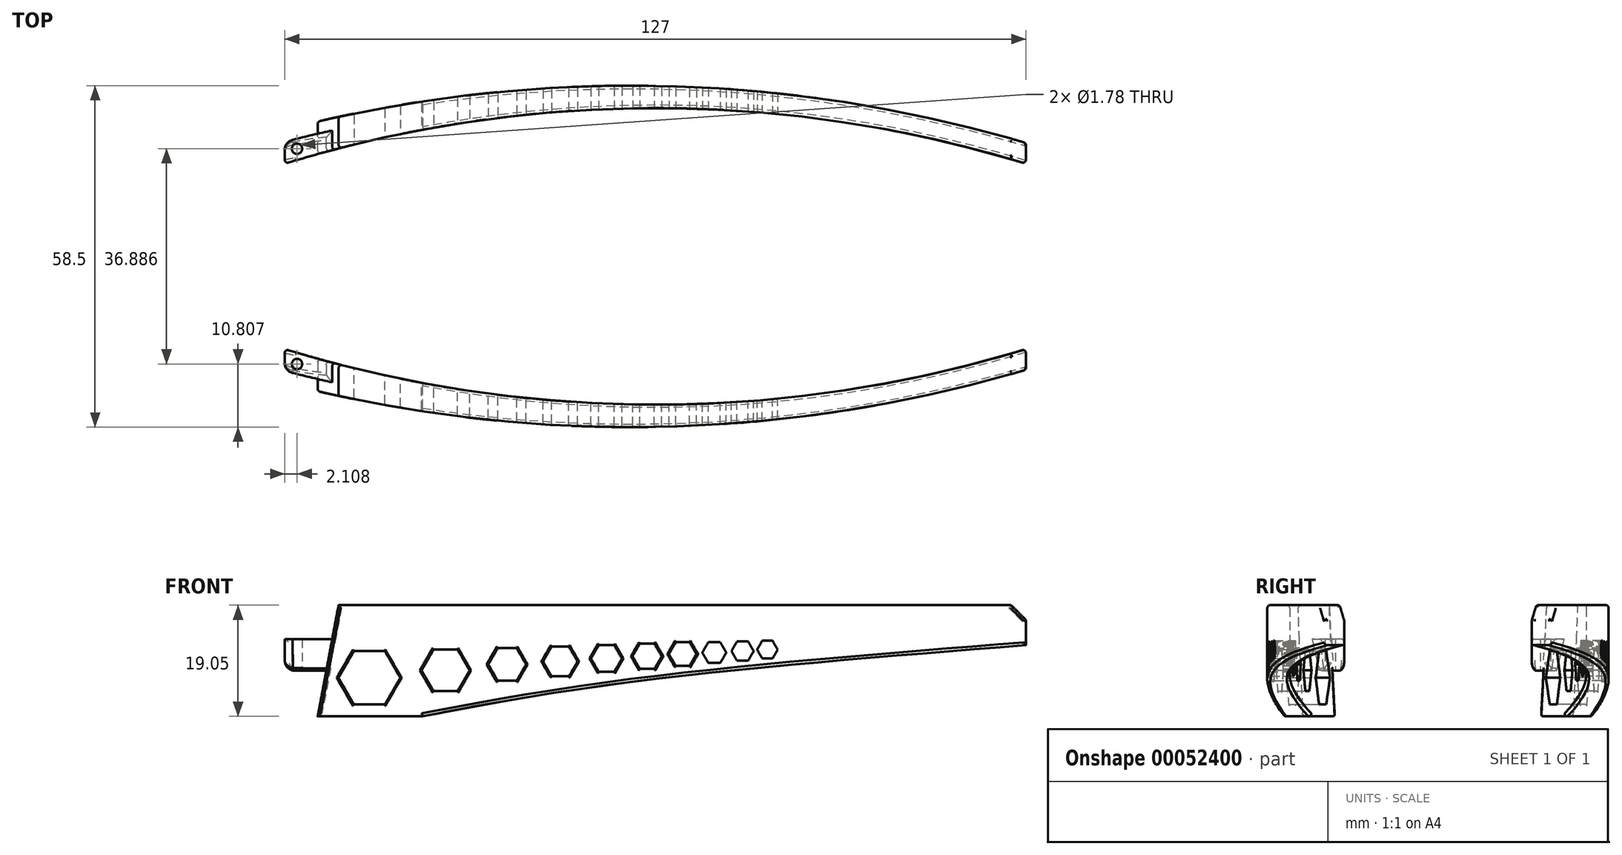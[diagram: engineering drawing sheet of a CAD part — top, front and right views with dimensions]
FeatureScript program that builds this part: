
annotation { "Feature Type Name" : "Feature", "Feature Type Description" : "" }
export const myFeature = defineFeature(function(context is Context, id is Id, definition is map)
    precondition{}
    {
        {
            var Q0;
            Q0=qCreatedBy(makeId("Top.planeOp"),FACE);
            var sketch = newSketch(context, id + "F0", { "sketchPlane" : qUnion([Q0])});
            skLineSegment(sketch, "E0.bottom", {"start": v(0, 0) * mm, "end": v(127, 0) * mm});
            skLineSegment(sketch, "E0.top", {"start": v(0, -9.53) * mm, "end": v(127, -9.53) * mm});
            skLineSegment(sketch, "E0.left", {"start": v(0, 0) * mm, "end": v(0, -9.53) * mm});
            skLineSegment(sketch, "E0.right", {"start": v(127, 0) * mm, "end": v(127, -9.53) * mm});
            skPoint(sketch, "E1", {"position": v(63.5, 0) * mm});
            skArc(sketch, "E2", {"start": v(127, -9.53) * mm, "mid": v(63.5, 0) * mm, "end": v(0, -9.53) * mm});
            skPoint(sketch, "E3", {"position": v(0, -3.68) * mm});
            skPoint(sketch, "E4", {"position": v(63.5, 3.81) * mm});
            skPoint(sketch, "E5", {"position": v(127, -5.97) * mm});
            skArc(sketch, "E6", {"start": v(127, -5.97) * mm, "mid": v(63.66, 3.8) * mm, "end": v(0, -3.68) * mm});
            skSolve(sketch);
        }
        {
            var Q0;
            {var subQ0=sQuery(id+"F0.wireOp",EDGE,"E6");var subQ1=sQuery(id+"F0.wireOp",EDGE,"E0.bottom");var subQ2=makeQuery(id+"F0.imprint","INTERSECT",VERTEX,{"disambiguationData":[OD(0.0)],"derivedFrom":[subQ1,subQ0]});Q0=makeQuery(id+"F0.imprint","IMPRINT",FACE,{"disambiguationData":[TD([[makeQuery(id+"F0.imprint","IMPRINT",EDGE,{"disambiguationData":[TD([[subQ2,-1.0]])],"derivedFrom":subQ1}),1.0]])]});}
            var Q1;
            {var subQ0=sQuery(id+"F0.wireOp",EDGE,"E6");var subQ1=sQuery(id+"F0.wireOp",EDGE,"E0.bottom");var subQ2=makeQuery(id+"F0.imprint","INTERSECT",VERTEX,{"disambiguationData":[OD(0.0)],"derivedFrom":[subQ1,subQ0]});Q1=makeQuery(id+"F0.imprint","IMPRINT",FACE,{"disambiguationData":[TD([[makeQuery(id+"F0.imprint","IMPRINT",EDGE,{"disambiguationData":[TD([[subQ2,-1.0]])],"derivedFrom":subQ1}),-1.0]])]});}
            var Q2;
            {var subQ0=sQuery(id+"F0.wireOp",EDGE,"E6");var subQ1=sQuery(id+"F0.wireOp",EDGE,"E0.bottom");var subQ2=makeQuery(id+"F0.imprint","INTERSECT",VERTEX,{"disambiguationData":[OD(1.0)],"derivedFrom":[subQ1,subQ0]});Q2=makeQuery(id+"F0.imprint","IMPRINT",FACE,{"disambiguationData":[TD([[makeQuery(id+"F0.imprint","IMPRINT",EDGE,{"disambiguationData":[TD([[subQ2,1.0]])],"derivedFrom":subQ1}),-1.0]])]});}
            extrude(context, id + "F1", {"entities" : qUnion([Q0, Q1, Q2]), "depth" : 19.05 * mm});
        }
        {
            var Q0;
            Q0=qCreatedBy(makeId("Front.planeOp"),FACE);
            var sketch = newSketch(context, id + "F2", { "sketchPlane" : qUnion([Q0])});
            skLineSegment(sketch, "E7.0.0", {"start": v(127, 0) * mm, "end": v(0, 0) * mm});
            skLineSegment(sketch, "E7.0.1", {"start": v(127, 0) * mm, "end": v(127, 19.05) * mm});
            skLineSegment(sketch, "E7.0.2", {"start": v(0, 19.05) * mm, "end": v(127, 19.05) * mm});
            skLineSegment(sketch, "E7.0.3", {"start": v(0, 19.05) * mm, "end": v(0, 0) * mm});
            skPoint(sketch, "E8", {"position": v(7.11, 7.82) * mm});
            skPoint(sketch, "E9", {"position": v(8.13, 13.2) * mm});
            skLineSegment(sketch, "E10", {"start": v(8.13, 13.2) * mm, "end": v(0, 13.2) * mm});
            skLineSegment(sketch, "E11", {"start": v(7.11, 7.82) * mm, "end": v(0, 7.82) * mm});
            skLineSegment(sketch, "E12", {"start": v(8.13, 13.2) * mm, "end": v(7.11, 7.82) * mm});
            skLineSegment(sketch, "E13", {"start": v(8.13, 13.2) * mm, "end": v(9.23, 19.05) * mm});
            skLineSegment(sketch, "E14", {"start": v(7.11, 7.82) * mm, "end": v(5.64, 0) * mm});
            skLineSegment(sketch, "E15", {"start": v(8.13, 13.2) * mm, "end": v(127, 13.2) * mm, "construction": true});
            skLineSegment(sketch, "E16", {"start": v(11.8, 0) * mm, "end": v(20.08, 0) * mm});
            skCircle(sketch, "E17.cCircle", {"center": v(14.5, 6.6) * mm, "radius": 7.63 * mm, "construction": true});
            skLineSegment(sketch, "E17.0", {"start": v(6.88, 6.6) * mm, "end": v(10.7, 13.2) * mm});
            skLineSegment(sketch, "E17.1", {"start": v(10.7, 13.2) * mm, "end": v(18.32, 13.2) * mm});
            skLineSegment(sketch, "E17.2", {"start": v(18.32, 13.2) * mm, "end": v(22.13, 6.6) * mm});
            skLineSegment(sketch, "E17.3", {"start": v(22.13, 6.6) * mm, "end": v(18.32, 0) * mm});
            skLineSegment(sketch, "E17.4", {"start": v(18.32, 0) * mm, "end": v(10.7, 0) * mm});
            skLineSegment(sketch, "E17.5", {"start": v(10.7, 0) * mm, "end": v(6.88, 6.6) * mm});
            skCircle(sketch, "E18.cCircle", {"center": v(27.56, 7.87) * mm, "radius": 6.16 * mm, "construction": true});
            skLineSegment(sketch, "E18.0", {"start": v(21.4, 7.87) * mm, "end": v(24.48, 13.2) * mm});
            skLineSegment(sketch, "E18.1", {"start": v(24.48, 13.2) * mm, "end": v(30.64, 13.2) * mm});
            skLineSegment(sketch, "E18.2", {"start": v(30.64, 13.2) * mm, "end": v(33.72, 7.87) * mm});
            skLineSegment(sketch, "E18.3", {"start": v(33.72, 7.87) * mm, "end": v(30.64, 2.54) * mm});
            skLineSegment(sketch, "E18.4", {"start": v(30.64, 2.54) * mm, "end": v(24.48, 2.54) * mm});
            skLineSegment(sketch, "E18.5", {"start": v(24.48, 2.54) * mm, "end": v(21.4, 7.87) * mm});
            skCircle(sketch, "E19.cCircle", {"center": v(38.12, 8.89) * mm, "radius": 4.99 * mm, "construction": true});
            skLineSegment(sketch, "E19.0", {"start": v(33.13, 8.89) * mm, "end": v(35.62, 13.2) * mm});
            skLineSegment(sketch, "E19.1", {"start": v(35.62, 13.2) * mm, "end": v(40.61, 13.2) * mm});
            skLineSegment(sketch, "E19.2", {"start": v(40.61, 13.2) * mm, "end": v(43.1, 8.89) * mm});
            skLineSegment(sketch, "E19.3", {"start": v(43.1, 8.89) * mm, "end": v(40.61, 4.57) * mm});
            skLineSegment(sketch, "E19.4", {"start": v(40.61, 4.57) * mm, "end": v(35.62, 4.57) * mm});
            skLineSegment(sketch, "E19.5", {"start": v(35.62, 4.57) * mm, "end": v(33.13, 8.89) * mm});
            skCircle(sketch, "E20.cCircle", {"center": v(47.2, 9.4) * mm, "radius": 4.4 * mm, "construction": true});
            skLineSegment(sketch, "E20.0", {"start": v(42.81, 9.4) * mm, "end": v(45.01, 13.2) * mm});
            skLineSegment(sketch, "E20.1", {"start": v(45.01, 13.2) * mm, "end": v(49.4, 13.2) * mm});
            skLineSegment(sketch, "E20.2", {"start": v(49.4, 13.2) * mm, "end": v(51.6, 9.4) * mm});
            skLineSegment(sketch, "E20.3", {"start": v(51.6, 9.4) * mm, "end": v(49.4, 5.59) * mm});
            skLineSegment(sketch, "E20.4", {"start": v(49.4, 5.59) * mm, "end": v(45.01, 5.59) * mm});
            skLineSegment(sketch, "E20.5", {"start": v(45.01, 5.59) * mm, "end": v(42.81, 9.4) * mm});
            skCircle(sketch, "E21.cCircle", {"center": v(55.13, 9.9) * mm, "radius": 3.81 * mm, "construction": true});
            skLineSegment(sketch, "E21.0", {"start": v(51.32, 9.9) * mm, "end": v(53.22, 13.2) * mm});
            skLineSegment(sketch, "E21.1", {"start": v(53.22, 13.2) * mm, "end": v(57.04, 13.2) * mm});
            skLineSegment(sketch, "E21.2", {"start": v(57.04, 13.2) * mm, "end": v(58.94, 9.9) * mm});
            skLineSegment(sketch, "E21.3", {"start": v(58.94, 9.9) * mm, "end": v(57.04, 6.6) * mm});
            skLineSegment(sketch, "E21.4", {"start": v(57.04, 6.6) * mm, "end": v(53.22, 6.6) * mm});
            skLineSegment(sketch, "E21.5", {"start": v(53.22, 6.6) * mm, "end": v(51.32, 9.9) * mm});
            skCircle(sketch, "E22.cCircle", {"center": v(62.1, 10.29) * mm, "radius": 3.37 * mm, "construction": true});
            skLineSegment(sketch, "E22.0", {"start": v(58.72, 10.29) * mm, "end": v(60.4, 13.2) * mm});
            skLineSegment(sketch, "E22.1", {"start": v(60.4, 13.2) * mm, "end": v(63.78, 13.2) * mm});
            skLineSegment(sketch, "E22.2", {"start": v(63.78, 13.2) * mm, "end": v(65.47, 10.29) * mm});
            skLineSegment(sketch, "E22.3", {"start": v(65.47, 10.29) * mm, "end": v(63.78, 7.37) * mm});
            skLineSegment(sketch, "E22.4", {"start": v(63.78, 7.37) * mm, "end": v(60.4, 7.37) * mm});
            skLineSegment(sketch, "E22.5", {"start": v(60.4, 7.37) * mm, "end": v(58.72, 10.29) * mm});
            skCircle(sketch, "E23.cCircle", {"center": v(68.18, 10.67) * mm, "radius": 2.93 * mm, "construction": true});
            skLineSegment(sketch, "E23.0", {"start": v(65.25, 10.67) * mm, "end": v(66.71, 13.2) * mm});
            skLineSegment(sketch, "E23.1", {"start": v(66.71, 13.2) * mm, "end": v(69.65, 13.2) * mm});
            skLineSegment(sketch, "E23.2", {"start": v(69.65, 13.2) * mm, "end": v(71.11, 10.67) * mm});
            skLineSegment(sketch, "E23.3", {"start": v(71.11, 10.67) * mm, "end": v(69.65, 8.13) * mm});
            skLineSegment(sketch, "E23.4", {"start": v(69.65, 8.13) * mm, "end": v(66.71, 8.13) * mm});
            skLineSegment(sketch, "E23.5", {"start": v(66.71, 8.13) * mm, "end": v(65.25, 10.67) * mm});
            skCircle(sketch, "E24.cCircle", {"center": v(73.6, 10.92) * mm, "radius": 2.64 * mm, "construction": true});
            skLineSegment(sketch, "E24.0", {"start": v(70.97, 10.92) * mm, "end": v(72.29, 13.2) * mm});
            skLineSegment(sketch, "E24.1", {"start": v(72.29, 13.2) * mm, "end": v(74.93, 13.2) * mm});
            skLineSegment(sketch, "E24.2", {"start": v(74.93, 13.2) * mm, "end": v(76.25, 10.92) * mm});
            skLineSegment(sketch, "E24.3", {"start": v(76.25, 10.92) * mm, "end": v(74.93, 8.64) * mm});
            skLineSegment(sketch, "E24.4", {"start": v(74.93, 8.64) * mm, "end": v(72.29, 8.64) * mm});
            skLineSegment(sketch, "E24.5", {"start": v(72.29, 8.64) * mm, "end": v(70.97, 10.92) * mm});
            skCircle(sketch, "E25.cCircle", {"center": v(78.45, 11.18) * mm, "radius": 2.35 * mm, "construction": true});
            skLineSegment(sketch, "E25.0", {"start": v(76.1, 11.18) * mm, "end": v(77.27, 13.2) * mm});
            skLineSegment(sketch, "E25.1", {"start": v(77.27, 13.2) * mm, "end": v(79.62, 13.2) * mm});
            skLineSegment(sketch, "E25.2", {"start": v(79.62, 13.2) * mm, "end": v(80.8, 11.18) * mm});
            skLineSegment(sketch, "E25.3", {"start": v(80.8, 11.18) * mm, "end": v(79.62, 9.14) * mm});
            skLineSegment(sketch, "E25.4", {"start": v(79.62, 9.14) * mm, "end": v(77.27, 9.14) * mm});
            skLineSegment(sketch, "E25.5", {"start": v(77.27, 9.14) * mm, "end": v(76.1, 11.18) * mm});
            skCircle(sketch, "E26.cCircle", {"center": v(82.7, 11.43) * mm, "radius": 2.05 * mm, "construction": true});
            skLineSegment(sketch, "E26.0", {"start": v(80.65, 11.43) * mm, "end": v(81.67, 13.2) * mm});
            skLineSegment(sketch, "E26.1", {"start": v(81.67, 13.2) * mm, "end": v(83.72, 13.2) * mm});
            skLineSegment(sketch, "E26.2", {"start": v(83.72, 13.2) * mm, "end": v(84.75, 11.43) * mm});
            skLineSegment(sketch, "E26.3", {"start": v(84.75, 11.43) * mm, "end": v(83.72, 9.65) * mm});
            skLineSegment(sketch, "E26.4", {"start": v(83.72, 9.65) * mm, "end": v(81.67, 9.65) * mm});
            skLineSegment(sketch, "E26.5", {"start": v(81.67, 9.65) * mm, "end": v(80.65, 11.43) * mm});
            skFitSpline(sketch, "E27", {"points": [v(127, 13.2) * mm, v(57.04, 6.6) * mm, v(18.32, 0) * mm], "startDerivative": vector(-131.36, -10.43) * mm, "endDerivative": vector(-83.7, -16.27) * mm});
            skLineSegment(sketch, "E28.0", {"start": v(10.7, 11.18) * mm, "end": v(18.32, 11.18) * mm, "construction": true});
            skLineSegment(sketch, "E29.0", {"start": v(24.48, 11.43) * mm, "end": v(30.64, 11.43) * mm, "construction": true});
            skLineSegment(sketch, "E30.0", {"start": v(35.62, 11.68) * mm, "end": v(40.61, 11.68) * mm, "construction": true});
            skLineSegment(sketch, "E31.0", {"start": v(45.01, 11.94) * mm, "end": v(49.4, 11.94) * mm, "construction": true});
            skLineSegment(sketch, "E32.0", {"start": v(53.22, 12.2) * mm, "end": v(57.04, 12.2) * mm, "construction": true});
            skLineSegment(sketch, "E33.0", {"start": v(60.4, 12.45) * mm, "end": v(63.78, 12.45) * mm, "construction": true});
            skLineSegment(sketch, "E34.0", {"start": v(66.71, 12.7) * mm, "end": v(69.65, 12.7) * mm, "construction": true});
            skLineSegment(sketch, "E35.0", {"start": v(72.29, 12.7) * mm, "end": v(74.93, 12.7) * mm, "construction": true});
            skLineSegment(sketch, "E36.0", {"start": v(77.27, 12.83) * mm, "end": v(79.62, 12.83) * mm, "construction": true});
            skLineSegment(sketch, "E37.0", {"start": v(81.67, 12.95) * mm, "end": v(83.72, 12.95) * mm, "construction": true});
            skCircle(sketch, "E38.cCircle", {"center": v(14.5, 6.6) * mm, "radius": 4.57 * mm, "construction": true});
            skLineSegment(sketch, "E38.0", {"start": v(11.87, 11.18) * mm, "end": v(17.15, 11.18) * mm});
            skLineSegment(sketch, "E38.1", {"start": v(17.15, 11.18) * mm, "end": v(19.79, 6.6) * mm});
            skLineSegment(sketch, "E38.2", {"start": v(19.79, 6.6) * mm, "end": v(17.15, 2.03) * mm});
            skLineSegment(sketch, "E38.3", {"start": v(17.15, 2.03) * mm, "end": v(11.87, 2.03) * mm});
            skLineSegment(sketch, "E38.4", {"start": v(11.87, 2.03) * mm, "end": v(9.23, 6.6) * mm});
            skLineSegment(sketch, "E38.5", {"start": v(9.23, 6.6) * mm, "end": v(11.87, 11.18) * mm});
            skPoint(sketch, "E38.0.midPoint", {"position": v(14.5, 11.18) * mm});
            skCircle(sketch, "E39.cCircle", {"center": v(27.56, 7.87) * mm, "radius": 3.56 * mm, "construction": true});
            skLineSegment(sketch, "E39.0", {"start": v(25.5, 11.43) * mm, "end": v(29.61, 11.43) * mm});
            skLineSegment(sketch, "E39.1", {"start": v(29.61, 11.43) * mm, "end": v(31.67, 7.87) * mm});
            skLineSegment(sketch, "E39.2", {"start": v(31.67, 7.87) * mm, "end": v(29.61, 4.32) * mm});
            skLineSegment(sketch, "E39.3", {"start": v(29.61, 4.32) * mm, "end": v(25.5, 4.32) * mm});
            skLineSegment(sketch, "E39.4", {"start": v(25.5, 4.32) * mm, "end": v(23.45, 7.87) * mm});
            skLineSegment(sketch, "E39.5", {"start": v(23.45, 7.87) * mm, "end": v(25.5, 11.43) * mm});
            skPoint(sketch, "E39.0.midPoint", {"position": v(27.56, 11.43) * mm});
            skCircle(sketch, "E40.cCircle", {"center": v(38.12, 8.89) * mm, "radius": 2.8 * mm, "construction": true});
            skLineSegment(sketch, "E40.0", {"start": v(36.5, 11.68) * mm, "end": v(39.73, 11.68) * mm});
            skLineSegment(sketch, "E40.1", {"start": v(39.73, 11.68) * mm, "end": v(41.34, 8.89) * mm});
            skLineSegment(sketch, "E40.2", {"start": v(41.34, 8.89) * mm, "end": v(39.73, 6.1) * mm});
            skLineSegment(sketch, "E40.3", {"start": v(39.73, 6.1) * mm, "end": v(36.5, 6.1) * mm});
            skLineSegment(sketch, "E40.4", {"start": v(36.5, 6.1) * mm, "end": v(34.9, 8.89) * mm});
            skLineSegment(sketch, "E40.5", {"start": v(34.9, 8.89) * mm, "end": v(36.5, 11.68) * mm});
            skPoint(sketch, "E40.0.midPoint", {"position": v(38.12, 11.68) * mm});
            skCircle(sketch, "E41.cCircle", {"center": v(47.2, 9.4) * mm, "radius": 2.54 * mm, "construction": true});
            skLineSegment(sketch, "E41.0", {"start": v(45.74, 11.94) * mm, "end": v(48.68, 11.94) * mm});
            skLineSegment(sketch, "E41.1", {"start": v(48.68, 11.94) * mm, "end": v(50.14, 9.4) * mm});
            skLineSegment(sketch, "E41.2", {"start": v(50.14, 9.4) * mm, "end": v(48.68, 6.86) * mm});
            skLineSegment(sketch, "E41.3", {"start": v(48.68, 6.86) * mm, "end": v(45.74, 6.86) * mm});
            skLineSegment(sketch, "E41.4", {"start": v(45.74, 6.86) * mm, "end": v(44.28, 9.4) * mm});
            skLineSegment(sketch, "E41.5", {"start": v(44.28, 9.4) * mm, "end": v(45.74, 11.94) * mm});
            skPoint(sketch, "E41.0.midPoint", {"position": v(47.2, 11.94) * mm});
            skCircle(sketch, "E42.cCircle", {"center": v(55.13, 9.9) * mm, "radius": 2.29 * mm, "construction": true});
            skLineSegment(sketch, "E42.0", {"start": v(53.8, 12.2) * mm, "end": v(56.45, 12.2) * mm});
            skLineSegment(sketch, "E42.1", {"start": v(56.45, 12.2) * mm, "end": v(57.77, 9.9) * mm});
            skLineSegment(sketch, "E42.2", {"start": v(57.77, 9.9) * mm, "end": v(56.45, 7.62) * mm});
            skLineSegment(sketch, "E42.3", {"start": v(56.45, 7.62) * mm, "end": v(53.8, 7.62) * mm});
            skLineSegment(sketch, "E42.4", {"start": v(53.8, 7.62) * mm, "end": v(52.49, 9.9) * mm});
            skLineSegment(sketch, "E42.5", {"start": v(52.49, 9.9) * mm, "end": v(53.8, 12.2) * mm});
            skPoint(sketch, "E42.0.midPoint", {"position": v(55.13, 12.2) * mm});
            skCircle(sketch, "E43.cCircle", {"center": v(62.1, 10.29) * mm, "radius": 2.16 * mm, "construction": true});
            skLineSegment(sketch, "E43.0", {"start": v(60.85, 12.45) * mm, "end": v(63.34, 12.45) * mm});
            skLineSegment(sketch, "E43.1", {"start": v(63.34, 12.45) * mm, "end": v(64.59, 10.29) * mm});
            skLineSegment(sketch, "E43.2", {"start": v(64.59, 10.29) * mm, "end": v(63.34, 8.13) * mm});
            skLineSegment(sketch, "E43.3", {"start": v(63.34, 8.13) * mm, "end": v(60.85, 8.13) * mm});
            skLineSegment(sketch, "E43.4", {"start": v(60.85, 8.13) * mm, "end": v(59.6, 10.29) * mm});
            skLineSegment(sketch, "E43.5", {"start": v(59.6, 10.29) * mm, "end": v(60.85, 12.45) * mm});
            skPoint(sketch, "E43.0.midPoint", {"position": v(62.1, 12.45) * mm});
            skCircle(sketch, "E44.cCircle", {"center": v(68.18, 10.67) * mm, "radius": 2.03 * mm, "construction": true});
            skLineSegment(sketch, "E44.0", {"start": v(67, 12.7) * mm, "end": v(69.35, 12.7) * mm});
            skLineSegment(sketch, "E44.1", {"start": v(69.35, 12.7) * mm, "end": v(70.53, 10.67) * mm});
            skLineSegment(sketch, "E44.2", {"start": v(70.53, 10.67) * mm, "end": v(69.35, 8.64) * mm});
            skLineSegment(sketch, "E44.3", {"start": v(69.35, 8.64) * mm, "end": v(67, 8.64) * mm});
            skLineSegment(sketch, "E44.4", {"start": v(67, 8.64) * mm, "end": v(65.83, 10.67) * mm});
            skLineSegment(sketch, "E44.5", {"start": v(65.83, 10.67) * mm, "end": v(67, 12.7) * mm});
            skPoint(sketch, "E44.0.midPoint", {"position": v(68.18, 12.7) * mm});
            skPoint(sketch, "E45.0.midPoint", {"position": v(73.6, 12.7) * mm});
            skPoint(sketch, "E46.0.midPoint", {"position": v(78.45, 12.83) * mm});
            skPoint(sketch, "E47.0.midPoint", {"position": v(82.7, 12.95) * mm});
            skFitSpline(sketch, "E48.0", {"points": [v(127.08, 12.2) * mm, v(121.6, 11.76) * mm, v(110.66, 10.9) * mm, v(94.57, 9.55) * mm, v(81.71, 8.36) * mm, v(71.92, 7.36) * mm, v(64.86, 6.57) * mm, v(58.12, 5.74) * mm, v(51.76, 4.86) * mm, v(45.73, 3.95) * mm, v(38.04, 2.68) * mm, v(28.97, 1.04) * mm, v(22, -0.32) * mm, v(18.51, -1) * mm]});
            skCircle(sketch, "E49.cCircle", {"center": v(73.6, 10.92) * mm, "radius": 1.78 * mm, "construction": true});
            skLineSegment(sketch, "E49.0", {"start": v(72.58, 12.7) * mm, "end": v(74.63, 12.7) * mm});
            skLineSegment(sketch, "E49.1", {"start": v(74.63, 12.7) * mm, "end": v(75.66, 10.92) * mm});
            skLineSegment(sketch, "E49.2", {"start": v(75.66, 10.92) * mm, "end": v(74.63, 9.14) * mm});
            skLineSegment(sketch, "E49.3", {"start": v(74.63, 9.14) * mm, "end": v(72.58, 9.14) * mm});
            skLineSegment(sketch, "E49.4", {"start": v(72.58, 9.14) * mm, "end": v(71.55, 10.92) * mm});
            skLineSegment(sketch, "E49.5", {"start": v(71.55, 10.92) * mm, "end": v(72.58, 12.7) * mm});
            skCircle(sketch, "E50.cCircle", {"center": v(78.45, 11.18) * mm, "radius": 1.65 * mm, "construction": true});
            skLineSegment(sketch, "E50.0", {"start": v(77.5, 12.83) * mm, "end": v(79.4, 12.83) * mm});
            skLineSegment(sketch, "E50.1", {"start": v(79.4, 12.83) * mm, "end": v(80.35, 11.18) * mm});
            skLineSegment(sketch, "E50.2", {"start": v(80.35, 11.18) * mm, "end": v(79.4, 9.52) * mm});
            skLineSegment(sketch, "E50.3", {"start": v(79.4, 9.53) * mm, "end": v(77.5, 9.52) * mm});
            skLineSegment(sketch, "E50.4", {"start": v(77.5, 9.52) * mm, "end": v(76.54, 11.18) * mm});
            skLineSegment(sketch, "E50.5", {"start": v(76.54, 11.18) * mm, "end": v(77.5, 12.83) * mm});
            skCircle(sketch, "E51.cCircle", {"center": v(82.7, 11.43) * mm, "radius": 1.52 * mm, "construction": true});
            skLineSegment(sketch, "E51.0", {"start": v(81.82, 12.95) * mm, "end": v(83.58, 12.95) * mm});
            skLineSegment(sketch, "E51.1", {"start": v(83.58, 12.95) * mm, "end": v(84.46, 11.43) * mm});
            skLineSegment(sketch, "E51.2", {"start": v(84.46, 11.43) * mm, "end": v(83.58, 9.9) * mm});
            skLineSegment(sketch, "E51.3", {"start": v(83.58, 9.9) * mm, "end": v(81.82, 9.9) * mm});
            skLineSegment(sketch, "E51.4", {"start": v(81.82, 9.9) * mm, "end": v(80.94, 11.43) * mm});
            skLineSegment(sketch, "E51.5", {"start": v(80.94, 11.43) * mm, "end": v(81.82, 12.95) * mm});
            skSolve(sketch);
        }
        {
            var Q0;
            {var subQ4=sQuery(id+"F2.wireOp",EDGE,"E10");Q0=makeQuery(id+"F2.imprint","IMPRINT",FACE,{"disambiguationData":[TD([[makeQuery(id+"F2.imprint","IMPRINT",EDGE,{"derivedFrom":subQ4}),-1.0]])]});}
            var Q1;
            {var subQ4=sQuery(id+"F2.wireOp",EDGE,"E11");Q1=makeQuery(id+"F2.imprint","IMPRINT",FACE,{"disambiguationData":[TD([[makeQuery(id+"F2.imprint","IMPRINT",EDGE,{"derivedFrom":subQ4}),1.0]])]});}
            extrude(context, id + "F3", {"entities" : qUnion([Q0, Q1]), "operationType" : NewBodyOperationType.REMOVE, "endBound" : BoundingType.THROUGH_ALL, "depth" : 25.4 * mm});
        }
        {
            var Q0;
            {var subQ0=sQuery(id+"F2.wireOp",EDGE,"E7.0.1");var subQ1=sQuery(id+"F2.wireOp",EDGE,"E7.0.0");var subQ2=makeQuery(id+"F2.imprint","INTERSECT",VERTEX,{"derivedFrom":[subQ1,subQ0]});Q0=makeQuery(id+"F2.imprint","IMPRINT",FACE,{"disambiguationData":[TD([[makeQuery(id+"F2.imprint","IMPRINT",EDGE,{"disambiguationData":[TD([[subQ2,-1.0]])],"derivedFrom":subQ1}),-1.0]])]});}
            extrude(context, id + "F4", {"entities" : qUnion([Q0]), "operationType" : NewBodyOperationType.REMOVE, "endBound" : BoundingType.SYMMETRIC, "oppositeDirection" : true, "depth" : 25.4 * mm});
        }
        {
            var Q0;
            Q0=makeQuery(id+"F1.opExtrude","CAP_EDGE",EDGE,{"disambiguationData":[OSD([sQuery(id+"F0.wireOp",EDGE,"E0.right")])],"isStart":false});
            var Q1;
            Q1=makeQuery(id+"F4.boolean.opBoolean","COPY",EDGE,{"derivedFrom":makeQuery(id+"F4.opExtrude","SWEPT_EDGE",EDGE,{"disambiguationData":[OSD([sQuery(id+"F2.wireOp",EDGE,"E7.0.1"),sQuery(id+"F2.wireOp",EDGE,"E27")])]})});
            chamfer(context, id + "F5", {"entities" : qUnion([Q0, Q1]), "width" : 2.54 * mm, "tangentPropagation" : true});
        }
        {
            var Q0;
            Q0=makeQuery(id+"F2.imprint","IMPRINT",FACE,{"disambiguationData":[TD([[makeQuery(id+"F2.imprint","IMPRINT",EDGE,{"derivedFrom":sQuery(id+"F2.wireOp",EDGE,"E38.0")}),-1.0]])]});
            var Q1;
            Q1=makeQuery(id+"F2.imprint","IMPRINT",FACE,{"disambiguationData":[TD([[makeQuery(id+"F2.imprint","IMPRINT",EDGE,{"derivedFrom":sQuery(id+"F2.wireOp",EDGE,"E39.0")}),-1.0]])]});
            var Q2;
            Q2=makeQuery(id+"F2.imprint","IMPRINT",FACE,{"disambiguationData":[TD([[makeQuery(id+"F2.imprint","IMPRINT",EDGE,{"derivedFrom":sQuery(id+"F2.wireOp",EDGE,"E40.0")}),-1.0]])]});
            var Q3;
            Q3=makeQuery(id+"F2.imprint","IMPRINT",FACE,{"disambiguationData":[TD([[makeQuery(id+"F2.imprint","IMPRINT",EDGE,{"derivedFrom":sQuery(id+"F2.wireOp",EDGE,"E41.0")}),-1.0]])]});
            var Q4;
            Q4=makeQuery(id+"F2.imprint","IMPRINT",FACE,{"disambiguationData":[TD([[makeQuery(id+"F2.imprint","IMPRINT",EDGE,{"derivedFrom":sQuery(id+"F2.wireOp",EDGE,"E43.0")}),-1.0]])]});
            var Q5;
            Q5=makeQuery(id+"F2.imprint","IMPRINT",FACE,{"disambiguationData":[TD([[makeQuery(id+"F2.imprint","IMPRINT",EDGE,{"derivedFrom":sQuery(id+"F2.wireOp",EDGE,"E42.0")}),-1.0]])]});
            var Q6;
            Q6=makeQuery(id+"F2.imprint","IMPRINT",FACE,{"disambiguationData":[TD([[makeQuery(id+"F2.imprint","IMPRINT",EDGE,{"derivedFrom":sQuery(id+"F2.wireOp",EDGE,"E44.0")}),-1.0]])]});
            var Q7;
            Q7=makeQuery(id+"F2.imprint","IMPRINT",FACE,{"disambiguationData":[TD([[makeQuery(id+"F2.imprint","IMPRINT",EDGE,{"derivedFrom":sQuery(id+"F2.wireOp",EDGE,"E49.0")}),-1.0]])]});
            var Q8;
            Q8=makeQuery(id+"F2.imprint","IMPRINT",FACE,{"disambiguationData":[TD([[makeQuery(id+"F2.imprint","IMPRINT",EDGE,{"derivedFrom":sQuery(id+"F2.wireOp",EDGE,"E50.0")}),-1.0]])]});
            var Q9;
            Q9=makeQuery(id+"F2.imprint","IMPRINT",FACE,{"disambiguationData":[TD([[makeQuery(id+"F2.imprint","IMPRINT",EDGE,{"derivedFrom":sQuery(id+"F2.wireOp",EDGE,"E51.0")}),-1.0]])]});
            extrude(context, id + "F6", {"entities" : qUnion([Q0, Q1, Q2, Q3, Q4, Q5, Q6, Q7, Q8, Q9]), "operationType" : NewBodyOperationType.REMOVE, "endBound" : BoundingType.SYMMETRIC, "oppositeDirection" : true, "depth" : 25.4 * mm});
        }
        {
            var Q0;
            Q0=makeQuery(id+"F6.boolean.opBoolean","INTERSECT",EDGE,{"derivedFrom":[makeQuery(id+"F1.opExtrude","SWEPT_FACE",FACE,{"disambiguationData":[OSD([sQuery(id+"F0.wireOp",EDGE,"E6")])]}),makeQuery(id+"F6.opExtrude","SWEPT_FACE",FACE,{"disambiguationData":[OSD([sQuery(id+"F2.wireOp",EDGE,"E38.4")])]})]});
            var Q1;
            Q1=makeQuery(id+"F6.boolean.opBoolean","INTERSECT",EDGE,{"derivedFrom":[makeQuery(id+"F1.opExtrude","SWEPT_FACE",FACE,{"disambiguationData":[OSD([sQuery(id+"F0.wireOp",EDGE,"E6")])]}),makeQuery(id+"F6.opExtrude","SWEPT_FACE",FACE,{"disambiguationData":[OSD([sQuery(id+"F2.wireOp",EDGE,"E38.5")])]})]});
            var Q2;
            Q2=makeQuery(id+"F6.boolean.opBoolean","INTERSECT",EDGE,{"derivedFrom":[makeQuery(id+"F1.opExtrude","SWEPT_FACE",FACE,{"disambiguationData":[OSD([sQuery(id+"F0.wireOp",EDGE,"E6")])]}),makeQuery(id+"F6.opExtrude","SWEPT_FACE",FACE,{"disambiguationData":[OSD([sQuery(id+"F2.wireOp",EDGE,"E38.0")])]})]});
            var Q3;
            Q3=makeQuery(id+"F6.boolean.opBoolean","INTERSECT",EDGE,{"derivedFrom":[makeQuery(id+"F1.opExtrude","SWEPT_FACE",FACE,{"disambiguationData":[OSD([sQuery(id+"F0.wireOp",EDGE,"E6")])]}),makeQuery(id+"F6.opExtrude","SWEPT_FACE",FACE,{"disambiguationData":[OSD([sQuery(id+"F2.wireOp",EDGE,"E38.1")])]})]});
            var Q4;
            Q4=makeQuery(id+"F6.boolean.opBoolean","INTERSECT",EDGE,{"derivedFrom":[makeQuery(id+"F1.opExtrude","SWEPT_FACE",FACE,{"disambiguationData":[OSD([sQuery(id+"F0.wireOp",EDGE,"E6")])]}),makeQuery(id+"F6.opExtrude","SWEPT_FACE",FACE,{"disambiguationData":[OSD([sQuery(id+"F2.wireOp",EDGE,"E38.2")])]})]});
            var Q5;
            Q5=makeQuery(id+"F6.boolean.opBoolean","INTERSECT",EDGE,{"derivedFrom":[makeQuery(id+"F1.opExtrude","SWEPT_FACE",FACE,{"disambiguationData":[OSD([sQuery(id+"F0.wireOp",EDGE,"E6")])]}),makeQuery(id+"F6.opExtrude","SWEPT_FACE",FACE,{"disambiguationData":[OSD([sQuery(id+"F2.wireOp",EDGE,"E38.3")])]})]});
            var Q6;
            Q6=makeQuery(id+"F6.boolean.opBoolean","INTERSECT",EDGE,{"derivedFrom":[makeQuery(id+"F1.opExtrude","SWEPT_FACE",FACE,{"disambiguationData":[OSD([sQuery(id+"F0.wireOp",EDGE,"E6")])]}),makeQuery(id+"F6.opExtrude","SWEPT_FACE",FACE,{"disambiguationData":[OSD([sQuery(id+"F2.wireOp",EDGE,"E39.4")])]})]});
            var Q7;
            Q7=makeQuery(id+"F6.boolean.opBoolean","INTERSECT",EDGE,{"derivedFrom":[makeQuery(id+"F1.opExtrude","SWEPT_FACE",FACE,{"disambiguationData":[OSD([sQuery(id+"F0.wireOp",EDGE,"E6")])]}),makeQuery(id+"F6.opExtrude","SWEPT_FACE",FACE,{"disambiguationData":[OSD([sQuery(id+"F2.wireOp",EDGE,"E39.3")])]})]});
            var Q8;
            Q8=makeQuery(id+"F6.boolean.opBoolean","INTERSECT",EDGE,{"derivedFrom":[makeQuery(id+"F1.opExtrude","SWEPT_FACE",FACE,{"disambiguationData":[OSD([sQuery(id+"F0.wireOp",EDGE,"E6")])]}),makeQuery(id+"F6.opExtrude","SWEPT_FACE",FACE,{"disambiguationData":[OSD([sQuery(id+"F2.wireOp",EDGE,"E39.2")])]})]});
            var Q9;
            Q9=makeQuery(id+"F6.boolean.opBoolean","INTERSECT",EDGE,{"derivedFrom":[makeQuery(id+"F1.opExtrude","SWEPT_FACE",FACE,{"disambiguationData":[OSD([sQuery(id+"F0.wireOp",EDGE,"E6")])]}),makeQuery(id+"F6.opExtrude","SWEPT_FACE",FACE,{"disambiguationData":[OSD([sQuery(id+"F2.wireOp",EDGE,"E39.1")])]})]});
            var Q10;
            Q10=makeQuery(id+"F6.boolean.opBoolean","INTERSECT",EDGE,{"derivedFrom":[makeQuery(id+"F1.opExtrude","SWEPT_FACE",FACE,{"disambiguationData":[OSD([sQuery(id+"F0.wireOp",EDGE,"E6")])]}),makeQuery(id+"F6.opExtrude","SWEPT_FACE",FACE,{"disambiguationData":[OSD([sQuery(id+"F2.wireOp",EDGE,"E39.0")])]})]});
            var Q11;
            Q11=makeQuery(id+"F6.boolean.opBoolean","INTERSECT",EDGE,{"derivedFrom":[makeQuery(id+"F1.opExtrude","SWEPT_FACE",FACE,{"disambiguationData":[OSD([sQuery(id+"F0.wireOp",EDGE,"E6")])]}),makeQuery(id+"F6.opExtrude","SWEPT_FACE",FACE,{"disambiguationData":[OSD([sQuery(id+"F2.wireOp",EDGE,"E39.5")])]})]});
            var Q12;
            Q12=makeQuery(id+"F6.boolean.opBoolean","INTERSECT",EDGE,{"derivedFrom":[makeQuery(id+"F1.opExtrude","SWEPT_FACE",FACE,{"disambiguationData":[OSD([sQuery(id+"F0.wireOp",EDGE,"E6")])]}),makeQuery(id+"F6.opExtrude","SWEPT_FACE",FACE,{"disambiguationData":[OSD([sQuery(id+"F2.wireOp",EDGE,"E40.4")])]})]});
            var Q13;
            Q13=makeQuery(id+"F6.boolean.opBoolean","INTERSECT",EDGE,{"derivedFrom":[makeQuery(id+"F1.opExtrude","SWEPT_FACE",FACE,{"disambiguationData":[OSD([sQuery(id+"F0.wireOp",EDGE,"E6")])]}),makeQuery(id+"F6.opExtrude","SWEPT_FACE",FACE,{"disambiguationData":[OSD([sQuery(id+"F2.wireOp",EDGE,"E40.3")])]})]});
            var Q14;
            Q14=makeQuery(id+"F6.boolean.opBoolean","INTERSECT",EDGE,{"derivedFrom":[makeQuery(id+"F1.opExtrude","SWEPT_FACE",FACE,{"disambiguationData":[OSD([sQuery(id+"F0.wireOp",EDGE,"E6")])]}),makeQuery(id+"F6.opExtrude","SWEPT_FACE",FACE,{"disambiguationData":[OSD([sQuery(id+"F2.wireOp",EDGE,"E40.2")])]})]});
            var Q15;
            Q15=makeQuery(id+"F6.boolean.opBoolean","INTERSECT",EDGE,{"derivedFrom":[makeQuery(id+"F1.opExtrude","SWEPT_FACE",FACE,{"disambiguationData":[OSD([sQuery(id+"F0.wireOp",EDGE,"E6")])]}),makeQuery(id+"F6.opExtrude","SWEPT_FACE",FACE,{"disambiguationData":[OSD([sQuery(id+"F2.wireOp",EDGE,"E40.1")])]})]});
            var Q16;
            Q16=makeQuery(id+"F6.boolean.opBoolean","INTERSECT",EDGE,{"derivedFrom":[makeQuery(id+"F1.opExtrude","SWEPT_FACE",FACE,{"disambiguationData":[OSD([sQuery(id+"F0.wireOp",EDGE,"E6")])]}),makeQuery(id+"F6.opExtrude","SWEPT_FACE",FACE,{"disambiguationData":[OSD([sQuery(id+"F2.wireOp",EDGE,"E40.0")])]})]});
            var Q17;
            Q17=makeQuery(id+"F6.boolean.opBoolean","INTERSECT",EDGE,{"derivedFrom":[makeQuery(id+"F1.opExtrude","SWEPT_FACE",FACE,{"disambiguationData":[OSD([sQuery(id+"F0.wireOp",EDGE,"E6")])]}),makeQuery(id+"F6.opExtrude","SWEPT_FACE",FACE,{"disambiguationData":[OSD([sQuery(id+"F2.wireOp",EDGE,"E40.5")])]})]});
            var Q18;
            Q18=makeQuery(id+"F6.boolean.opBoolean","INTERSECT",EDGE,{"derivedFrom":[makeQuery(id+"F1.opExtrude","SWEPT_FACE",FACE,{"disambiguationData":[OSD([sQuery(id+"F0.wireOp",EDGE,"E6")])]}),makeQuery(id+"F6.opExtrude","SWEPT_FACE",FACE,{"disambiguationData":[OSD([sQuery(id+"F2.wireOp",EDGE,"E41.4")])]})]});
            var Q19;
            Q19=makeQuery(id+"F6.boolean.opBoolean","INTERSECT",EDGE,{"derivedFrom":[makeQuery(id+"F1.opExtrude","SWEPT_FACE",FACE,{"disambiguationData":[OSD([sQuery(id+"F0.wireOp",EDGE,"E6")])]}),makeQuery(id+"F6.opExtrude","SWEPT_FACE",FACE,{"disambiguationData":[OSD([sQuery(id+"F2.wireOp",EDGE,"E41.3")])]})]});
            var Q20;
            Q20=makeQuery(id+"F6.boolean.opBoolean","INTERSECT",EDGE,{"derivedFrom":[makeQuery(id+"F1.opExtrude","SWEPT_FACE",FACE,{"disambiguationData":[OSD([sQuery(id+"F0.wireOp",EDGE,"E6")])]}),makeQuery(id+"F6.opExtrude","SWEPT_FACE",FACE,{"disambiguationData":[OSD([sQuery(id+"F2.wireOp",EDGE,"E41.2")])]})]});
            var Q21;
            Q21=makeQuery(id+"F6.boolean.opBoolean","INTERSECT",EDGE,{"derivedFrom":[makeQuery(id+"F1.opExtrude","SWEPT_FACE",FACE,{"disambiguationData":[OSD([sQuery(id+"F0.wireOp",EDGE,"E6")])]}),makeQuery(id+"F6.opExtrude","SWEPT_FACE",FACE,{"disambiguationData":[OSD([sQuery(id+"F2.wireOp",EDGE,"E41.1")])]})]});
            var Q22;
            Q22=makeQuery(id+"F6.boolean.opBoolean","INTERSECT",EDGE,{"derivedFrom":[makeQuery(id+"F1.opExtrude","SWEPT_FACE",FACE,{"disambiguationData":[OSD([sQuery(id+"F0.wireOp",EDGE,"E6")])]}),makeQuery(id+"F6.opExtrude","SWEPT_FACE",FACE,{"disambiguationData":[OSD([sQuery(id+"F2.wireOp",EDGE,"E41.0")])]})]});
            var Q23;
            Q23=makeQuery(id+"F6.boolean.opBoolean","INTERSECT",EDGE,{"derivedFrom":[makeQuery(id+"F1.opExtrude","SWEPT_FACE",FACE,{"disambiguationData":[OSD([sQuery(id+"F0.wireOp",EDGE,"E6")])]}),makeQuery(id+"F6.opExtrude","SWEPT_FACE",FACE,{"disambiguationData":[OSD([sQuery(id+"F2.wireOp",EDGE,"E41.5")])]})]});
            var Q24;
            Q24=makeQuery(id+"F6.boolean.opBoolean","INTERSECT",EDGE,{"derivedFrom":[makeQuery(id+"F1.opExtrude","SWEPT_FACE",FACE,{"disambiguationData":[OSD([sQuery(id+"F0.wireOp",EDGE,"E6")])]}),makeQuery(id+"F6.opExtrude","SWEPT_FACE",FACE,{"disambiguationData":[OSD([sQuery(id+"F2.wireOp",EDGE,"E42.4")])]})]});
            var Q25;
            Q25=makeQuery(id+"F6.boolean.opBoolean","INTERSECT",EDGE,{"derivedFrom":[makeQuery(id+"F1.opExtrude","SWEPT_FACE",FACE,{"disambiguationData":[OSD([sQuery(id+"F0.wireOp",EDGE,"E6")])]}),makeQuery(id+"F6.opExtrude","SWEPT_FACE",FACE,{"disambiguationData":[OSD([sQuery(id+"F2.wireOp",EDGE,"E42.3")])]})]});
            var Q26;
            Q26=makeQuery(id+"F6.boolean.opBoolean","INTERSECT",EDGE,{"derivedFrom":[makeQuery(id+"F1.opExtrude","SWEPT_FACE",FACE,{"disambiguationData":[OSD([sQuery(id+"F0.wireOp",EDGE,"E6")])]}),makeQuery(id+"F6.opExtrude","SWEPT_FACE",FACE,{"disambiguationData":[OSD([sQuery(id+"F2.wireOp",EDGE,"E42.2")])]})]});
            var Q27;
            Q27=makeQuery(id+"F6.boolean.opBoolean","INTERSECT",EDGE,{"derivedFrom":[makeQuery(id+"F1.opExtrude","SWEPT_FACE",FACE,{"disambiguationData":[OSD([sQuery(id+"F0.wireOp",EDGE,"E6")])]}),makeQuery(id+"F6.opExtrude","SWEPT_FACE",FACE,{"disambiguationData":[OSD([sQuery(id+"F2.wireOp",EDGE,"E42.1")])]})]});
            var Q28;
            Q28=makeQuery(id+"F6.boolean.opBoolean","INTERSECT",EDGE,{"derivedFrom":[makeQuery(id+"F1.opExtrude","SWEPT_FACE",FACE,{"disambiguationData":[OSD([sQuery(id+"F0.wireOp",EDGE,"E6")])]}),makeQuery(id+"F6.opExtrude","SWEPT_FACE",FACE,{"disambiguationData":[OSD([sQuery(id+"F2.wireOp",EDGE,"E42.2")])]})]});
            var Q29;
            Q29=makeQuery(id+"F6.boolean.opBoolean","INTERSECT",EDGE,{"derivedFrom":[makeQuery(id+"F1.opExtrude","SWEPT_FACE",FACE,{"disambiguationData":[OSD([sQuery(id+"F0.wireOp",EDGE,"E6")])]}),makeQuery(id+"F6.opExtrude","SWEPT_FACE",FACE,{"disambiguationData":[OSD([sQuery(id+"F2.wireOp",EDGE,"E42.0")])]})]});
            var Q30;
            Q30=makeQuery(id+"F6.boolean.opBoolean","INTERSECT",EDGE,{"derivedFrom":[makeQuery(id+"F1.opExtrude","SWEPT_FACE",FACE,{"disambiguationData":[OSD([sQuery(id+"F0.wireOp",EDGE,"E6")])]}),makeQuery(id+"F6.opExtrude","SWEPT_FACE",FACE,{"disambiguationData":[OSD([sQuery(id+"F2.wireOp",EDGE,"E42.5")])]})]});
            var Q31;
            Q31=makeQuery(id+"F6.boolean.opBoolean","INTERSECT",EDGE,{"derivedFrom":[makeQuery(id+"F1.opExtrude","SWEPT_FACE",FACE,{"disambiguationData":[OSD([sQuery(id+"F0.wireOp",EDGE,"E6")])]}),makeQuery(id+"F6.opExtrude","SWEPT_FACE",FACE,{"disambiguationData":[OSD([sQuery(id+"F2.wireOp",EDGE,"E43.4")])]})]});
            var Q32;
            Q32=makeQuery(id+"F6.boolean.opBoolean","INTERSECT",EDGE,{"derivedFrom":[makeQuery(id+"F1.opExtrude","SWEPT_FACE",FACE,{"disambiguationData":[OSD([sQuery(id+"F0.wireOp",EDGE,"E6")])]}),makeQuery(id+"F6.opExtrude","SWEPT_FACE",FACE,{"disambiguationData":[OSD([sQuery(id+"F2.wireOp",EDGE,"E43.3")])]})]});
            var Q33;
            Q33=makeQuery(id+"F6.boolean.opBoolean","INTERSECT",EDGE,{"derivedFrom":[makeQuery(id+"F1.opExtrude","SWEPT_FACE",FACE,{"disambiguationData":[OSD([sQuery(id+"F0.wireOp",EDGE,"E6")])]}),makeQuery(id+"F6.opExtrude","SWEPT_FACE",FACE,{"disambiguationData":[OSD([sQuery(id+"F2.wireOp",EDGE,"E43.2")])]})]});
            var Q34;
            Q34=makeQuery(id+"F6.boolean.opBoolean","INTERSECT",EDGE,{"derivedFrom":[makeQuery(id+"F1.opExtrude","SWEPT_FACE",FACE,{"disambiguationData":[OSD([sQuery(id+"F0.wireOp",EDGE,"E6")])]}),makeQuery(id+"F6.opExtrude","SWEPT_FACE",FACE,{"disambiguationData":[OSD([sQuery(id+"F2.wireOp",EDGE,"E43.1")])]})]});
            var Q35;
            Q35=makeQuery(id+"F6.boolean.opBoolean","INTERSECT",EDGE,{"derivedFrom":[makeQuery(id+"F1.opExtrude","SWEPT_FACE",FACE,{"disambiguationData":[OSD([sQuery(id+"F0.wireOp",EDGE,"E6")])]}),makeQuery(id+"F6.opExtrude","SWEPT_FACE",FACE,{"disambiguationData":[OSD([sQuery(id+"F2.wireOp",EDGE,"E43.0")])]})]});
            var Q36;
            Q36=makeQuery(id+"F6.boolean.opBoolean","INTERSECT",EDGE,{"derivedFrom":[makeQuery(id+"F1.opExtrude","SWEPT_FACE",FACE,{"disambiguationData":[OSD([sQuery(id+"F0.wireOp",EDGE,"E6")])]}),makeQuery(id+"F6.opExtrude","SWEPT_FACE",FACE,{"disambiguationData":[OSD([sQuery(id+"F2.wireOp",EDGE,"E43.5")])]})]});
            var Q37;
            Q37=makeQuery(id+"F6.boolean.opBoolean","INTERSECT",EDGE,{"derivedFrom":[makeQuery(id+"F1.opExtrude","SWEPT_FACE",FACE,{"disambiguationData":[OSD([sQuery(id+"F0.wireOp",EDGE,"E6")])]}),makeQuery(id+"F6.opExtrude","SWEPT_FACE",FACE,{"disambiguationData":[OSD([sQuery(id+"F2.wireOp",EDGE,"E44.4")])]})]});
            var Q38;
            Q38=makeQuery(id+"F6.boolean.opBoolean","INTERSECT",EDGE,{"derivedFrom":[makeQuery(id+"F1.opExtrude","SWEPT_FACE",FACE,{"disambiguationData":[OSD([sQuery(id+"F0.wireOp",EDGE,"E6")])]}),makeQuery(id+"F6.opExtrude","SWEPT_FACE",FACE,{"disambiguationData":[OSD([sQuery(id+"F2.wireOp",EDGE,"E44.3")])]})]});
            var Q39;
            Q39=makeQuery(id+"F6.boolean.opBoolean","INTERSECT",EDGE,{"derivedFrom":[makeQuery(id+"F1.opExtrude","SWEPT_FACE",FACE,{"disambiguationData":[OSD([sQuery(id+"F0.wireOp",EDGE,"E6")])]}),makeQuery(id+"F6.opExtrude","SWEPT_FACE",FACE,{"disambiguationData":[OSD([sQuery(id+"F2.wireOp",EDGE,"E44.2")])]})]});
            var Q40;
            Q40=makeQuery(id+"F6.boolean.opBoolean","INTERSECT",EDGE,{"derivedFrom":[makeQuery(id+"F1.opExtrude","SWEPT_FACE",FACE,{"disambiguationData":[OSD([sQuery(id+"F0.wireOp",EDGE,"E6")])]}),makeQuery(id+"F6.opExtrude","SWEPT_FACE",FACE,{"disambiguationData":[OSD([sQuery(id+"F2.wireOp",EDGE,"E44.1")])]})]});
            var Q41;
            Q41=makeQuery(id+"F6.boolean.opBoolean","INTERSECT",EDGE,{"derivedFrom":[makeQuery(id+"F1.opExtrude","SWEPT_FACE",FACE,{"disambiguationData":[OSD([sQuery(id+"F0.wireOp",EDGE,"E6")])]}),makeQuery(id+"F6.opExtrude","SWEPT_FACE",FACE,{"disambiguationData":[OSD([sQuery(id+"F2.wireOp",EDGE,"E44.0")])]})]});
            var Q42;
            Q42=makeQuery(id+"F6.boolean.opBoolean","INTERSECT",EDGE,{"derivedFrom":[makeQuery(id+"F1.opExtrude","SWEPT_FACE",FACE,{"disambiguationData":[OSD([sQuery(id+"F0.wireOp",EDGE,"E6")])]}),makeQuery(id+"F6.opExtrude","SWEPT_FACE",FACE,{"disambiguationData":[OSD([sQuery(id+"F2.wireOp",EDGE,"E44.5")])]})]});
            var Q43;
            Q43=makeQuery(id+"F6.boolean.opBoolean","INTERSECT",EDGE,{"derivedFrom":[makeQuery(id+"F1.opExtrude","SWEPT_FACE",FACE,{"disambiguationData":[OSD([sQuery(id+"F0.wireOp",EDGE,"E6")])]}),makeQuery(id+"F6.opExtrude","SWEPT_FACE",FACE,{"disambiguationData":[OSD([sQuery(id+"F2.wireOp",EDGE,"E44.1")])]})]});
            var Q44;
            Q44=makeQuery(id+"F6.boolean.opBoolean","INTERSECT",EDGE,{"derivedFrom":[makeQuery(id+"F1.opExtrude","SWEPT_FACE",FACE,{"disambiguationData":[OSD([sQuery(id+"F0.wireOp",EDGE,"E6")])]}),makeQuery(id+"F6.opExtrude","SWEPT_FACE",FACE,{"disambiguationData":[OSD([sQuery(id+"F2.wireOp",EDGE,"E45.4")])]})]});
            var Q45;
            Q45=makeQuery(id+"F6.boolean.opBoolean","INTERSECT",EDGE,{"derivedFrom":[makeQuery(id+"F1.opExtrude","SWEPT_FACE",FACE,{"disambiguationData":[OSD([sQuery(id+"F0.wireOp",EDGE,"E6")])]}),makeQuery(id+"F6.opExtrude","SWEPT_FACE",FACE,{"disambiguationData":[OSD([sQuery(id+"F2.wireOp",EDGE,"E45.3")])]})]});
            var Q46;
            Q46=makeQuery(id+"F6.boolean.opBoolean","INTERSECT",EDGE,{"derivedFrom":[makeQuery(id+"F1.opExtrude","SWEPT_FACE",FACE,{"disambiguationData":[OSD([sQuery(id+"F0.wireOp",EDGE,"E6")])]}),makeQuery(id+"F6.opExtrude","SWEPT_FACE",FACE,{"disambiguationData":[OSD([sQuery(id+"F2.wireOp",EDGE,"E45.2")])]})]});
            var Q47;
            Q47=makeQuery(id+"F6.boolean.opBoolean","INTERSECT",EDGE,{"derivedFrom":[makeQuery(id+"F1.opExtrude","SWEPT_FACE",FACE,{"disambiguationData":[OSD([sQuery(id+"F0.wireOp",EDGE,"E6")])]}),makeQuery(id+"F6.opExtrude","SWEPT_FACE",FACE,{"disambiguationData":[OSD([sQuery(id+"F2.wireOp",EDGE,"E45.1")])]})]});
            var Q48;
            Q48=makeQuery(id+"F6.boolean.opBoolean","INTERSECT",EDGE,{"derivedFrom":[makeQuery(id+"F1.opExtrude","SWEPT_FACE",FACE,{"disambiguationData":[OSD([sQuery(id+"F0.wireOp",EDGE,"E6")])]}),makeQuery(id+"F6.opExtrude","SWEPT_FACE",FACE,{"disambiguationData":[OSD([sQuery(id+"F2.wireOp",EDGE,"E45.0")])]})]});
            var Q49;
            Q49=makeQuery(id+"F6.boolean.opBoolean","INTERSECT",EDGE,{"derivedFrom":[makeQuery(id+"F1.opExtrude","SWEPT_FACE",FACE,{"disambiguationData":[OSD([sQuery(id+"F0.wireOp",EDGE,"E6")])]}),makeQuery(id+"F6.opExtrude","SWEPT_FACE",FACE,{"disambiguationData":[OSD([sQuery(id+"F2.wireOp",EDGE,"E45.5")])]})]});
            var Q50;
            Q50=makeQuery(id+"F6.boolean.opBoolean","INTERSECT",EDGE,{"derivedFrom":[makeQuery(id+"F1.opExtrude","SWEPT_FACE",FACE,{"disambiguationData":[OSD([sQuery(id+"F0.wireOp",EDGE,"E6")])]}),makeQuery(id+"F6.opExtrude","SWEPT_FACE",FACE,{"disambiguationData":[OSD([sQuery(id+"F2.wireOp",EDGE,"E46.4")])]})]});
            var Q51;
            Q51=makeQuery(id+"F6.boolean.opBoolean","INTERSECT",EDGE,{"derivedFrom":[makeQuery(id+"F1.opExtrude","SWEPT_FACE",FACE,{"disambiguationData":[OSD([sQuery(id+"F0.wireOp",EDGE,"E6")])]}),makeQuery(id+"F6.opExtrude","SWEPT_FACE",FACE,{"disambiguationData":[OSD([sQuery(id+"F2.wireOp",EDGE,"E46.3")])]})]});
            var Q52;
            Q52=makeQuery(id+"F6.boolean.opBoolean","INTERSECT",EDGE,{"derivedFrom":[makeQuery(id+"F1.opExtrude","SWEPT_FACE",FACE,{"disambiguationData":[OSD([sQuery(id+"F0.wireOp",EDGE,"E6")])]}),makeQuery(id+"F6.opExtrude","SWEPT_FACE",FACE,{"disambiguationData":[OSD([sQuery(id+"F2.wireOp",EDGE,"E46.2")])]})]});
            var Q53;
            Q53=makeQuery(id+"F6.boolean.opBoolean","INTERSECT",EDGE,{"derivedFrom":[makeQuery(id+"F1.opExtrude","SWEPT_FACE",FACE,{"disambiguationData":[OSD([sQuery(id+"F0.wireOp",EDGE,"E6")])]}),makeQuery(id+"F6.opExtrude","SWEPT_FACE",FACE,{"disambiguationData":[OSD([sQuery(id+"F2.wireOp",EDGE,"E46.1")])]})]});
            var Q54;
            Q54=makeQuery(id+"F6.boolean.opBoolean","INTERSECT",EDGE,{"derivedFrom":[makeQuery(id+"F1.opExtrude","SWEPT_FACE",FACE,{"disambiguationData":[OSD([sQuery(id+"F0.wireOp",EDGE,"E6")])]}),makeQuery(id+"F6.opExtrude","SWEPT_FACE",FACE,{"disambiguationData":[OSD([sQuery(id+"F2.wireOp",EDGE,"E46.0")])]})]});
            var Q55;
            Q55=makeQuery(id+"F6.boolean.opBoolean","INTERSECT",EDGE,{"derivedFrom":[makeQuery(id+"F1.opExtrude","SWEPT_FACE",FACE,{"disambiguationData":[OSD([sQuery(id+"F0.wireOp",EDGE,"E6")])]}),makeQuery(id+"F6.opExtrude","SWEPT_FACE",FACE,{"disambiguationData":[OSD([sQuery(id+"F2.wireOp",EDGE,"E46.5")])]})]});
            var Q56;
            Q56=makeQuery(id+"F6.boolean.opBoolean","INTERSECT",EDGE,{"derivedFrom":[makeQuery(id+"F1.opExtrude","SWEPT_FACE",FACE,{"disambiguationData":[OSD([sQuery(id+"F0.wireOp",EDGE,"E6")])]}),makeQuery(id+"F6.opExtrude","SWEPT_FACE",FACE,{"disambiguationData":[OSD([sQuery(id+"F2.wireOp",EDGE,"E47.4")])]})]});
            var Q57;
            Q57=makeQuery(id+"F6.boolean.opBoolean","INTERSECT",EDGE,{"derivedFrom":[makeQuery(id+"F1.opExtrude","SWEPT_FACE",FACE,{"disambiguationData":[OSD([sQuery(id+"F0.wireOp",EDGE,"E6")])]}),makeQuery(id+"F6.opExtrude","SWEPT_FACE",FACE,{"disambiguationData":[OSD([sQuery(id+"F2.wireOp",EDGE,"E47.3")])]})]});
            var Q58;
            Q58=makeQuery(id+"F6.boolean.opBoolean","INTERSECT",EDGE,{"derivedFrom":[makeQuery(id+"F1.opExtrude","SWEPT_FACE",FACE,{"disambiguationData":[OSD([sQuery(id+"F0.wireOp",EDGE,"E6")])]}),makeQuery(id+"F6.opExtrude","SWEPT_FACE",FACE,{"disambiguationData":[OSD([sQuery(id+"F2.wireOp",EDGE,"E47.2")])]})]});
            var Q59;
            Q59=makeQuery(id+"F6.boolean.opBoolean","INTERSECT",EDGE,{"derivedFrom":[makeQuery(id+"F1.opExtrude","SWEPT_FACE",FACE,{"disambiguationData":[OSD([sQuery(id+"F0.wireOp",EDGE,"E6")])]}),makeQuery(id+"F6.opExtrude","SWEPT_FACE",FACE,{"disambiguationData":[OSD([sQuery(id+"F2.wireOp",EDGE,"E47.1")])]})]});
            var Q60;
            Q60=makeQuery(id+"F6.boolean.opBoolean","INTERSECT",EDGE,{"derivedFrom":[makeQuery(id+"F1.opExtrude","SWEPT_FACE",FACE,{"disambiguationData":[OSD([sQuery(id+"F0.wireOp",EDGE,"E6")])]}),makeQuery(id+"F6.opExtrude","SWEPT_FACE",FACE,{"disambiguationData":[OSD([sQuery(id+"F2.wireOp",EDGE,"E47.0")])]})]});
            var Q61;
            Q61=makeQuery(id+"F6.boolean.opBoolean","INTERSECT",EDGE,{"derivedFrom":[makeQuery(id+"F1.opExtrude","SWEPT_FACE",FACE,{"disambiguationData":[OSD([sQuery(id+"F0.wireOp",EDGE,"E6")])]}),makeQuery(id+"F6.opExtrude","SWEPT_FACE",FACE,{"disambiguationData":[OSD([sQuery(id+"F2.wireOp",EDGE,"E47.5")])]})]});
            fillet(context, id + "F7", {"entities" : qUnion([Q0, Q1, Q2, Q3, Q4, Q5, Q6, Q7, Q8, Q9, Q10, Q11, Q12, Q13, Q14, Q15, Q16, Q17, Q18, Q19, Q20, Q21, Q22, Q23, Q24, Q25, Q26, Q27, Q28, Q29, Q30, Q31, Q32, Q33, Q34, Q35, Q36, Q37, Q38, Q39, Q40, Q41, Q42, Q43, Q44, Q45, Q46, Q47, Q48, Q49, Q50, Q51, Q52, Q53, Q54, Q55, Q56, Q57, Q58, Q59, Q60, Q61]), "radius" : 0.25 * mm, "tangentPropagation" : true, "allowEdgeOverflow" : false});
        }
        {
            var Q0;
            Q0=makeQuery(id+"F3.boolean.opBoolean","COPY",FACE,{"derivedFrom":makeQuery(id+"F3.opExtrude","SWEPT_FACE",FACE,{"disambiguationData":[OSD([sQuery(id+"F2.wireOp",EDGE,"E10")])]})});
            var sketch = newSketch(context, id + "F8", { "sketchPlane" : qUnion([Q0])});
            skLineSegment(sketch, "E52.0.0", {"start": v(0, -5.78) * mm, "end": v(0, -9.53) * mm});
            skArc(sketch, "E52.0.1", {"start": v(0, -9.53) * mm, "mid": v(4.05, -8.32) * mm, "end": v(8.13, -7.2) * mm});
            skLineSegment(sketch, "E52.0.2", {"start": v(8.13, -7.2) * mm, "end": v(8.13, 0.86) * mm, "construction": true});
            skArc(sketch, "E53.0", {"start": v(8.13, -3.82) * mm, "mid": v(0.86, -5.56) * mm, "end": v(-6.35, -7.53) * mm});
            skLineSegment(sketch, "E54.0", {"start": v(-6.35, -2.77) * mm, "end": v(-6.35, -7.53) * mm});
            skPoint(sketch, "E55.orphan", {"position": v(0, -3.68) * mm});
            skArc(sketch, "E56.0", {"start": v(8.13, 0.86) * mm, "mid": v(0.86, -0.84) * mm, "end": v(-6.35, -2.77) * mm});
            skLineSegment(sketch, "E57", {"start": v(8.13, -3.82) * mm, "end": v(8.13, 0.86) * mm});
            skSolve(sketch);
        }
        {
            var Q0;
            {var subQ1=sQuery(id+"F2.wireOp",EDGE,"E10");var subQ6=makeQuery(id+"F3.boolean.opBoolean","INTERSECT",EDGE,{"derivedFrom":[makeQuery(id+"F1.opExtrude","SWEPT_FACE",FACE,{"disambiguationData":[OSD([sQuery(id+"F0.wireOp",EDGE,"E6")])]}),makeQuery(id+"F3.opExtrude","SWEPT_FACE",FACE,{"disambiguationData":[OSD([subQ1])]})]});Q0=makeQuery(id+"F8.imprint","IMPRINT",FACE,{"disambiguationData":[TD([[makeQuery(id+"F8.imprint","IMPRINT",EDGE,{"derivedFrom":subQ6}),-1.0]])]});}
            var Q1;
            {var subQ4=sQuery(id+"F8.wireOp",EDGE,"E54.0");Q1=makeQuery(id+"F8.imprint","IMPRINT",FACE,{"disambiguationData":[TD([[makeQuery(id+"F8.imprint","IMPRINT",EDGE,{"derivedFrom":subQ4}),1.0]])]});}
            var Q2;
            Q2=sQuery(id+"F8.wireOp",EDGE,"E57");
            revolve(context, id + "F9", {"operationType" : NewBodyOperationType.REMOVE, "entities" : qUnion([Q0, Q1]), "axis" : qUnion([Q2]), "revolveType" : RevolveType.ONE_DIRECTION, "oppositeDirection" : true, "angle" : 79.32 * degree});
        }
        {
            var Q0;
            Q0=makeQuery(id+"F3.boolean.opBoolean","COPY",FACE,{"derivedFrom":makeQuery(id+"F3.opExtrude","SWEPT_FACE",FACE,{"disambiguationData":[OSD([sQuery(id+"F2.wireOp",EDGE,"E11")])]})});
            var sketch = newSketch(context, id + "F10", { "sketchPlane" : qUnion([Q0])});
            skPoint(sketch, "E58", {"position": v(2.1, 6.96) * mm});
            skSolve(sketch);
        }
        {
            var Q0;
            Q0=makeQuery(id+"F3.boolean.opBoolean","INTERSECT",EDGE,{"derivedFrom":[makeQuery(id+"F1.opExtrude","SWEPT_FACE",FACE,{"disambiguationData":[OSD([sQuery(id+"F0.wireOp",EDGE,"E2")])]}),makeQuery(id+"F3.opExtrude","SWEPT_FACE",FACE,{"disambiguationData":[OSD([sQuery(id+"F2.wireOp",EDGE,"E10")])]})]});
            var Q1;
            Q1=makeQuery(id+"F3.boolean.opBoolean","INTERSECT",EDGE,{"derivedFrom":[makeQuery(id+"F1.opExtrude","SWEPT_FACE",FACE,{"disambiguationData":[OSD([sQuery(id+"F0.wireOp",EDGE,"E2")])]}),makeQuery(id+"F3.opExtrude","SWEPT_FACE",FACE,{"disambiguationData":[OSD([sQuery(id+"F2.wireOp",EDGE,"E11")])]})]});
            var Q2;
            Q2=makeQuery(id+"F3.boolean.opBoolean","INTERSECT",EDGE,{"derivedFrom":[makeQuery(id+"F1.opExtrude","SWEPT_FACE",FACE,{"disambiguationData":[OSD([sQuery(id+"F0.wireOp",EDGE,"E2")])]}),makeQuery(id+"F3.opExtrude","SWEPT_FACE",FACE,{"disambiguationData":[OSD([sQuery(id+"F2.wireOp",EDGE,"E14")])]})]});
            var Q3;
            Q3=makeQuery(id+"F3.boolean.opBoolean","INTERSECT",EDGE,{"derivedFrom":[makeQuery(id+"F1.opExtrude","SWEPT_FACE",FACE,{"disambiguationData":[OSD([sQuery(id+"F0.wireOp",EDGE,"E2")])]}),makeQuery(id+"F3.opExtrude","SWEPT_FACE",FACE,{"disambiguationData":[OSD([sQuery(id+"F2.wireOp",EDGE,"E13")])]})]});
            var Q4;
            Q4=makeQuery(id+"F3.boolean.opBoolean","INTERSECT",EDGE,{"derivedFrom":[makeQuery(id+"F1.opExtrude","SWEPT_FACE",FACE,{"disambiguationData":[OSD([sQuery(id+"F0.wireOp",EDGE,"E6")])]}),makeQuery(id+"F3.opExtrude","SWEPT_FACE",FACE,{"disambiguationData":[OSD([sQuery(id+"F2.wireOp",EDGE,"E14")])]})]});
            var Q5;
            {var subQ0=sQuery(id+"F2.wireOp",EDGE,"E14");Q5=makeQuery(id+"F9.boolean.opBoolean","SPLIT",EDGE,{"disambiguationData":[TD([makeQuery(id+"F1.opExtrude","CAP_FACE",FACE,{"disambiguationData":[OSD([sQuery(id+"F0.wireOp",EDGE,"E0.left"),sQuery(id+"F0.wireOp",EDGE,"E0.right"),sQuery(id+"F0.wireOp",EDGE,"E2"),sQuery(id+"F0.wireOp",EDGE,"E6")])],"isStart":true}),makeQuery(id+"F3.boolean.opBoolean","COPY",FACE,{"derivedFrom":makeQuery(id+"F3.opExtrude","SWEPT_FACE",FACE,{"disambiguationData":[OSD([subQ0])]})})])],"derivedFrom":makeQuery(id+"F3.boolean.opBoolean","COPY",EDGE,{"derivedFrom":makeQuery(id+"F3.opExtrude","SWEPT_EDGE",EDGE,{"disambiguationData":[OSD([sQuery(id+"F2.wireOp",EDGE,"E7.0.0"),subQ0])]})})});}
            var Q6;
            Q6=makeQuery(id+"F9.boolean.opBoolean","INTERSECT",EDGE,{"derivedFrom":[makeQuery(id+"F1.opExtrude","SWEPT_FACE",FACE,{"disambiguationData":[OSD([sQuery(id+"F0.wireOp",EDGE,"E6")])]}),makeQuery(id+"F9.opRevolve","CAP_FACE",FACE,{"disambiguationData":[OSD([sQuery(id+"F8.wireOp",EDGE,"E53.0"),sQuery(id+"F8.wireOp",EDGE,"E54.0"),sQuery(id+"F8.wireOp",EDGE,"E56.0"),sQuery(id+"F8.wireOp",EDGE,"E57")])],"isStart":false})]});
            var Q7;
            Q7=makeQuery(id+"F9.boolean.opBoolean","COPY",EDGE,{"derivedFrom":makeQuery(id+"F9.opRevolve","CAP_EDGE",EDGE,{"disambiguationData":[OSD([sQuery(id+"F8.wireOp",EDGE,"E53.0")])],"isStart":true})});
            var Q8;
            Q8=makeQuery(id+"F9.boolean.opBoolean","INTERSECT",EDGE,{"derivedFrom":[makeQuery(id+"F3.boolean.opBoolean","COPY",FACE,{"derivedFrom":makeQuery(id+"F3.opExtrude","SWEPT_FACE",FACE,{"disambiguationData":[OSD([sQuery(id+"F2.wireOp",EDGE,"E11")])]})}),makeQuery(id+"F9.opRevolve","SWEPT_FACE",FACE,{"disambiguationData":[OSD([sQuery(id+"F8.wireOp",EDGE,"E53.0")])]})]});
            var Q9;
            Q9=makeQuery(id+"F3.boolean.opBoolean","COPY",EDGE,{"derivedFrom":makeQuery(id+"F3.opExtrude","SWEPT_EDGE",EDGE,{"disambiguationData":[OSD([sQuery(id+"F2.wireOp",EDGE,"E7.0.2"),sQuery(id+"F2.wireOp",EDGE,"E13")])]})});
            var Q10;
            Q10=makeQuery(id+"F1.opExtrude","CAP_EDGE",EDGE,{"disambiguationData":[OSD([sQuery(id+"F0.wireOp",EDGE,"E2")])],"isStart":false});
            var Q11;
            Q11=makeQuery(id+"F1.opExtrude","CAP_EDGE",EDGE,{"disambiguationData":[OSD([sQuery(id+"F0.wireOp",EDGE,"E6")])],"isStart":false});
            var Q12;
            Q12=makeQuery(id+"F1.opExtrude","CAP_EDGE",EDGE,{"disambiguationData":[OSD([sQuery(id+"F0.wireOp",EDGE,"E2")])],"isStart":true});
            var Q13;
            Q13=makeQuery(id+"F1.opExtrude","CAP_EDGE",EDGE,{"disambiguationData":[OSD([sQuery(id+"F0.wireOp",EDGE,"E6")])],"isStart":true});
            var Q14;
            Q14=makeQuery(id+"F4.boolean.opBoolean","INTERSECT",EDGE,{"derivedFrom":[makeQuery(id+"F1.opExtrude","SWEPT_FACE",FACE,{"disambiguationData":[OSD([sQuery(id+"F0.wireOp",EDGE,"E2")])]}),makeQuery(id+"F4.opExtrude","SWEPT_FACE",FACE,{"disambiguationData":[OSD([sQuery(id+"F2.wireOp",EDGE,"E48.0")])]})]});
            var Q15;
            Q15=makeQuery(id+"F4.boolean.opBoolean","INTERSECT",EDGE,{"derivedFrom":[makeQuery(id+"F1.opExtrude","SWEPT_FACE",FACE,{"disambiguationData":[OSD([sQuery(id+"F0.wireOp",EDGE,"E6")])]}),makeQuery(id+"F4.opExtrude","SWEPT_FACE",FACE,{"disambiguationData":[OSD([sQuery(id+"F2.wireOp",EDGE,"E48.0")])]})]});
            var Q16;
            Q16=makeQuery(id+"F4.boolean.opBoolean","COPY",EDGE,{"derivedFrom":makeQuery(id+"F4.opExtrude","SWEPT_EDGE",EDGE,{"disambiguationData":[OSD([sQuery(id+"F2.wireOp",EDGE,"E7.0.0"),sQuery(id+"F2.wireOp",EDGE,"E48.0")])]})});
            var Q17;
            {var subQ0=sQuery(id+"F0.wireOp",EDGE,"E0.right");Q17=makeQuery(id+"F5.opChamfer","BLEND_EDGE",EDGE,{"blendedFrom":[makeQuery(id+"F1.opExtrude","CAP_EDGE",EDGE,{"disambiguationData":[OSD([subQ0])],"isStart":false}),makeQuery(id+"F1.opExtrude","CAP_FACE",FACE,{"disambiguationData":[OSD([sQuery(id+"F0.wireOp",EDGE,"E0.left"),subQ0,sQuery(id+"F0.wireOp",EDGE,"E2"),sQuery(id+"F0.wireOp",EDGE,"E6")])],"isStart":false})],"blendedInto":[makeQuery(id+"F1.opExtrude","CAP_FACE",FACE,{"disambiguationData":[OSD([sQuery(id+"F0.wireOp",EDGE,"E0.left"),subQ0,sQuery(id+"F0.wireOp",EDGE,"E2"),sQuery(id+"F0.wireOp",EDGE,"E6")])],"isStart":false})]});}
            var Q18;
            Q18=makeQuery(id+"F5.opChamfer","BLEND_EDGE",EDGE,{"blendedFrom":[makeQuery(id+"F1.opExtrude","CAP_EDGE",EDGE,{"disambiguationData":[OSD([sQuery(id+"F0.wireOp",EDGE,"E0.right")])],"isStart":false}),makeQuery(id+"F1.opExtrude","SWEPT_FACE",FACE,{"disambiguationData":[OSD([sQuery(id+"F0.wireOp",EDGE,"E2")])]})],"blendedInto":[makeQuery(id+"F1.opExtrude","SWEPT_FACE",FACE,{"disambiguationData":[OSD([sQuery(id+"F0.wireOp",EDGE,"E2")])]})]});
            var Q19;
            Q19=makeQuery(id+"F5.opChamfer","BLEND_EDGE",EDGE,{"blendedFrom":[makeQuery(id+"F1.opExtrude","CAP_EDGE",EDGE,{"disambiguationData":[OSD([sQuery(id+"F0.wireOp",EDGE,"E0.right")])],"isStart":false}),makeQuery(id+"F1.opExtrude","SWEPT_FACE",FACE,{"disambiguationData":[OSD([sQuery(id+"F0.wireOp",EDGE,"E6")])]})],"blendedInto":[makeQuery(id+"F1.opExtrude","SWEPT_FACE",FACE,{"disambiguationData":[OSD([sQuery(id+"F0.wireOp",EDGE,"E6")])]})]});
            var Q20;
            {var subQ0=sQuery(id+"F2.wireOp",EDGE,"E48.0");Q20=makeQuery(id+"F5.opChamfer","BLEND_EDGE",EDGE,{"blendedFrom":[makeQuery(id+"F4.boolean.opBoolean","COPY",EDGE,{"derivedFrom":makeQuery(id+"F4.opExtrude","SWEPT_EDGE",EDGE,{"disambiguationData":[OSD([sQuery(id+"F2.wireOp",EDGE,"E7.0.1"),subQ0])]})}),makeQuery(id+"F4.boolean.opBoolean","COPY",FACE,{"derivedFrom":makeQuery(id+"F4.opExtrude","SWEPT_FACE",FACE,{"disambiguationData":[OSD([subQ0])]})})],"blendedInto":[makeQuery(id+"F4.boolean.opBoolean","COPY",FACE,{"derivedFrom":makeQuery(id+"F4.opExtrude","SWEPT_FACE",FACE,{"disambiguationData":[OSD([subQ0])]})})]});}
            var Q21;
            Q21=makeQuery(id+"F5.opChamfer","BLEND_EDGE",EDGE,{"blendedFrom":[makeQuery(id+"F4.boolean.opBoolean","COPY",EDGE,{"derivedFrom":makeQuery(id+"F4.opExtrude","SWEPT_EDGE",EDGE,{"disambiguationData":[OSD([sQuery(id+"F2.wireOp",EDGE,"E7.0.1"),sQuery(id+"F2.wireOp",EDGE,"E48.0")])]})}),makeQuery(id+"F1.opExtrude","SWEPT_FACE",FACE,{"disambiguationData":[OSD([sQuery(id+"F0.wireOp",EDGE,"E6")])]})],"blendedInto":[makeQuery(id+"F1.opExtrude","SWEPT_FACE",FACE,{"disambiguationData":[OSD([sQuery(id+"F0.wireOp",EDGE,"E6")])]})]});
            var Q22;
            Q22=makeQuery(id+"F5.opChamfer","BLEND_EDGE",EDGE,{"blendedFrom":[makeQuery(id+"F4.boolean.opBoolean","COPY",EDGE,{"derivedFrom":makeQuery(id+"F4.opExtrude","SWEPT_EDGE",EDGE,{"disambiguationData":[OSD([sQuery(id+"F2.wireOp",EDGE,"E7.0.1"),sQuery(id+"F2.wireOp",EDGE,"E48.0")])]})}),makeQuery(id+"F1.opExtrude","SWEPT_FACE",FACE,{"disambiguationData":[OSD([sQuery(id+"F0.wireOp",EDGE,"E2")])]})],"blendedInto":[makeQuery(id+"F1.opExtrude","SWEPT_FACE",FACE,{"disambiguationData":[OSD([sQuery(id+"F0.wireOp",EDGE,"E2")])]})]});
            var Q23;
            {var subQ0=sQuery(id+"F0.wireOp",EDGE,"E0.right");Q23=makeQuery(id+"F5.opChamfer","BLEND_EDGE",EDGE,{"blendedFrom":[makeQuery(id+"F1.opExtrude","CAP_EDGE",EDGE,{"disambiguationData":[OSD([subQ0])],"isStart":false}),makeQuery(id+"F1.opExtrude","SWEPT_FACE",FACE,{"disambiguationData":[OSD([subQ0])]})],"blendedInto":[makeQuery(id+"F1.opExtrude","SWEPT_FACE",FACE,{"disambiguationData":[OSD([subQ0])]})]});}
            var Q24;
            Q24=makeQuery(id+"F5.opChamfer","BLEND_EDGE",EDGE,{"blendedFrom":[makeQuery(id+"F4.boolean.opBoolean","COPY",EDGE,{"derivedFrom":makeQuery(id+"F4.opExtrude","SWEPT_EDGE",EDGE,{"disambiguationData":[OSD([sQuery(id+"F2.wireOp",EDGE,"E7.0.1"),sQuery(id+"F2.wireOp",EDGE,"E48.0")])]})}),makeQuery(id+"F1.opExtrude","SWEPT_FACE",FACE,{"disambiguationData":[OSD([sQuery(id+"F0.wireOp",EDGE,"E0.right")])]})],"blendedInto":[makeQuery(id+"F1.opExtrude","SWEPT_FACE",FACE,{"disambiguationData":[OSD([sQuery(id+"F0.wireOp",EDGE,"E0.right")])]})]});
            var Q25;
            Q25=makeQuery(id+"F1.opExtrude","SWEPT_EDGE",EDGE,{"disambiguationData":[OSD([sQuery(id+"F0.wireOp",EDGE,"E0.right"),sQuery(id+"F0.wireOp",EDGE,"E6")])]});
            var Q26;
            Q26=makeQuery(id+"F1.opExtrude","SWEPT_EDGE",EDGE,{"disambiguationData":[OSD([sQuery(id+"F0.wireOp",EDGE,"E0.top"),sQuery(id+"F0.wireOp",EDGE,"E0.right"),sQuery(id+"F0.wireOp",EDGE,"E2")])]});
            var Q27;
            Q27=makeQuery(id+"F3.boolean.opBoolean","COPY",EDGE,{"derivedFrom":makeQuery(id+"F3.opExtrude","SWEPT_EDGE",EDGE,{"disambiguationData":[OSD([sQuery(id+"F2.wireOp",EDGE,"E7.0.3"),sQuery(id+"F2.wireOp",EDGE,"E10")])]})});
            var Q28;
            Q28=makeQuery(id+"F1.opExtrude","SWEPT_EDGE",EDGE,{"disambiguationData":[OSD([sQuery(id+"F0.wireOp",EDGE,"E0.top"),sQuery(id+"F0.wireOp",EDGE,"E0.left"),sQuery(id+"F0.wireOp",EDGE,"E2")])]});
            var Q29;
            Q29=makeQuery(id+"F3.boolean.opBoolean","COPY",EDGE,{"derivedFrom":makeQuery(id+"F3.opExtrude","SWEPT_EDGE",EDGE,{"disambiguationData":[OSD([sQuery(id+"F2.wireOp",EDGE,"E7.0.3"),sQuery(id+"F2.wireOp",EDGE,"E11")])]})});
            fillet(context, id + "F11", {"entities" : qUnion([Q0, Q1, Q2, Q3, Q4, Q5, Q6, Q7, Q8, Q9, Q10, Q11, Q12, Q13, Q14, Q15, Q16, Q17, Q18, Q19, Q20, Q21, Q22, Q23, Q24, Q25, Q26, Q27, Q28, Q29]), "radius" : 0.5 * mm, "tangentPropagation" : true, "allowEdgeOverflow" : false});
        }
        {
            var Q0;
            Q0=makeQuery(id+"F9.boolean.opBoolean","INTERSECT",EDGE,{"derivedFrom":[makeQuery(id+"F1.opExtrude","SWEPT_FACE",FACE,{"disambiguationData":[OSD([sQuery(id+"F0.wireOp",EDGE,"E0.left")])]}),makeQuery(id+"F9.opRevolve","SWEPT_FACE",FACE,{"disambiguationData":[OSD([sQuery(id+"F8.wireOp",EDGE,"E53.0")])]})]});
            fillet(context, id + "F12", {"entities" : qUnion([Q0]), "radius" : 1.78 * mm, "tangentPropagation" : true, "allowEdgeOverflow" : false});
        }
        {
            var Q0;
            Q0=sQuery(id+"F10.wireOp",VERTEX,"E58");
            var Q1;
            Q1=makeQuery(id+"F1.opExtrude","SWEPT_BODY",BODY,{"disambiguationData":[OSD([sQuery(id+"F0.wireOp",EDGE,"E0.left"),sQuery(id+"F0.wireOp",EDGE,"E0.right"),sQuery(id+"F0.wireOp",EDGE,"E2"),sQuery(id+"F0.wireOp",EDGE,"E6")])]});
            hole(context, id + "F13", {"style" : HoleStyle.SIMPLE, "endStyle" : HoleEndStyle.THROUGH, "holeDiameter" : 1.78 * mm, "locations" : qUnion([Q0]), "scope" : qUnion([Q1]), "isTappedThrough" : true});
        }
        {
            var Q0;
            Q0=qCreatedBy(makeId("Front.planeOp"),FACE);
            cPlane(context, id + "F14", {"entities" : qUnion([Q0]), "cplaneType" : CPlaneType.OFFSET, "offset" : 25.4 * mm, "width" : 152.4 * mm, "height" : 152.4 * mm});
        }
        {
            var Q0;
            Q0=makeQuery(id+"F1.opExtrude","SWEPT_BODY",BODY,{"disambiguationData":[OSD([sQuery(id+"F0.wireOp",EDGE,"E0.left"),sQuery(id+"F0.wireOp",EDGE,"E0.right"),sQuery(id+"F0.wireOp",EDGE,"E2"),sQuery(id+"F0.wireOp",EDGE,"E6")])]});
            var Q1;
            Q1=qCreatedBy(id+"F14.planeOp",FACE);
            mirror(context, id + "F15", {"entities" : qUnion([Q0]), "mirrorPlane" : qUnion([Q1])});
        }
    });
